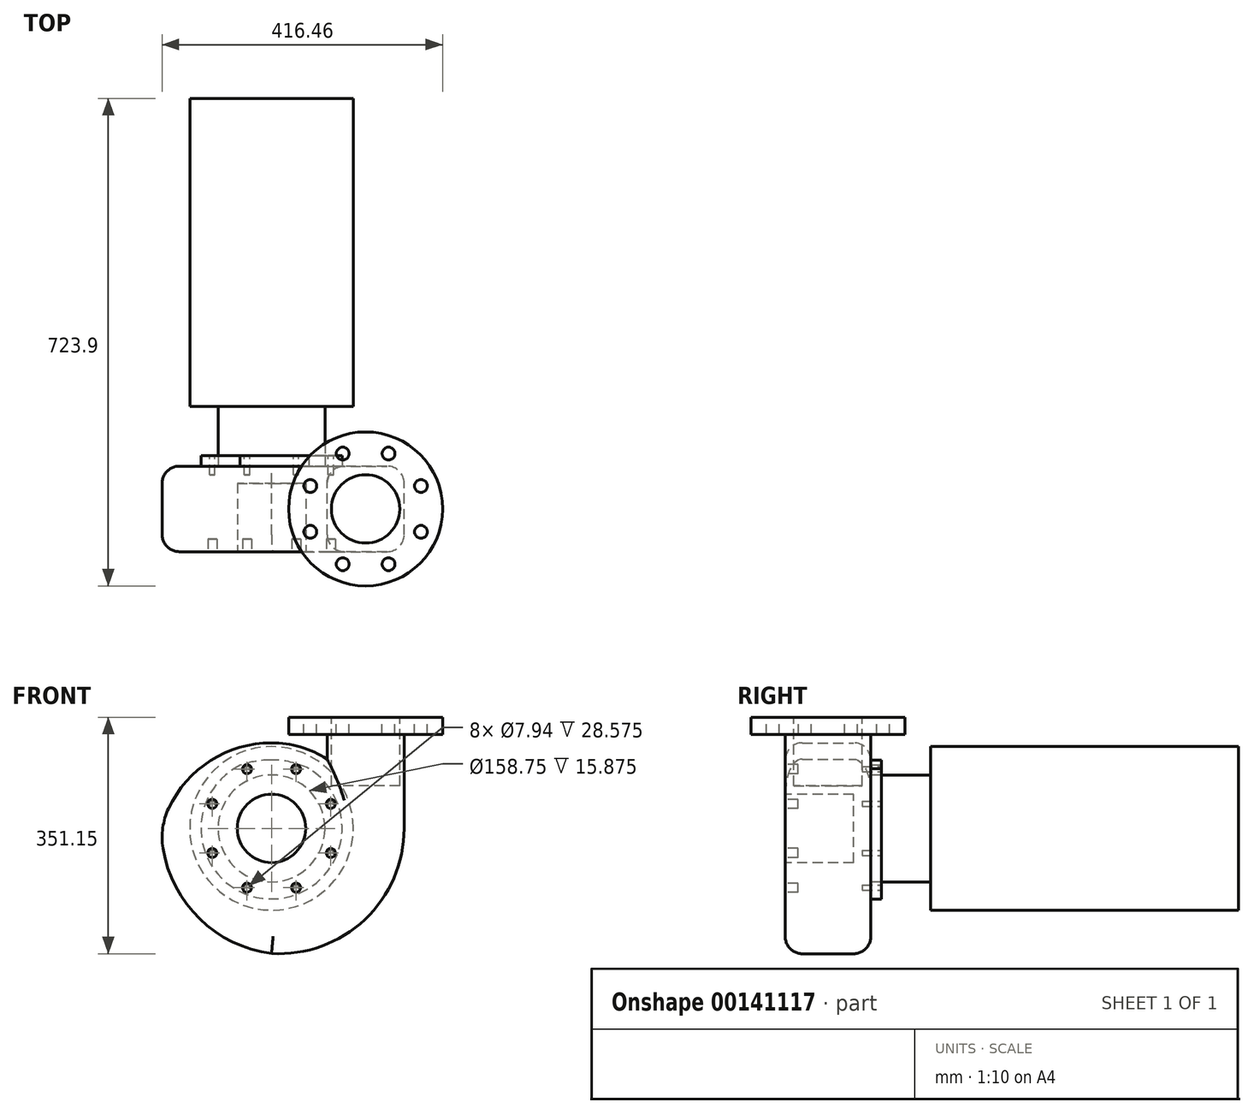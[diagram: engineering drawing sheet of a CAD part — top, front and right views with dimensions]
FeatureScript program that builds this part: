
annotation { "Feature Type Name" : "Feature", "Feature Type Description" : "" }
export const myFeature = defineFeature(function(context is Context, id is Id, definition is map)
    precondition{}
    {
        {
            var Q0;
            Q0=qCreatedBy(makeId("Front.planeOp"),FACE);
            var sketch = newSketch(context, id + "F0", { "sketchPlane" : qUnion([Q0])});
            skLineSegment(sketch, "E0", {"start": v(-163.51, 178.71) * mm, "end": v(-163.51, -178.71) * mm, "construction": true});
            skLineSegment(sketch, "E1", {"start": v(-233.34, 165.1) * mm, "end": v(383.82, 165.1) * mm, "construction": true});
            skLineSegment(sketch, "E2", {"start": v(-286.5, 127) * mm, "end": v(515.42, 127) * mm, "construction": true});
            skLineSegment(sketch, "E3", {"start": v(-378.23, 0) * mm, "end": v(533.77, 0) * mm, "construction": true});
            skLineSegment(sketch, "E4", {"start": v(0, 278.26) * mm, "end": v(0, -265.97) * mm, "construction": true});
            skLineSegment(sketch, "E5", {"start": v(-384.35, -185.74) * mm, "end": v(475.24, -185.74) * mm, "construction": true});
            skLineSegment(sketch, "E6", {"start": v(196.85, 265.15) * mm, "end": v(196.85, -251.12) * mm, "construction": true});
            skPoint(sketch, "E7", {"position": v(0, 0) * mm});
            skArc(sketch, "E8", {"start": v(-163.51, 0) * mm, "mid": v(-116.81, -123.73) * mm, "end": v(0, -185.74) * mm});
            skArc(sketch, "E9", {"start": v(0, -185.74) * mm, "mid": v(138.48, -135.32) * mm, "end": v(196.85, 0) * mm});
            skLineSegment(sketch, "E10", {"start": v(139.7, 277.34) * mm, "end": v(139.7, -312.69) * mm, "construction": true});
            skLineSegment(sketch, "E11", {"start": v(82.55, 361.3) * mm, "end": v(82.55, -345.34) * mm, "construction": true});
            skArc(sketch, "E12", {"start": v(0, 127) * mm, "mid": v(-103.52, 91.52) * mm, "end": v(-163.51, 0) * mm});
            skArc(sketch, "E13", {"start": v(139.7, 36.24) * mm, "mid": v(83.3, 102.32) * mm, "end": v(0, 127) * mm});
            skLineSegment(sketch, "E14", {"start": v(-450.42, 139.7) * mm, "end": v(521.7, 139.7) * mm, "construction": true});
            skLineSegment(sketch, "E15", {"start": v(196.85, 0) * mm, "end": v(196.85, 127) * mm});
            skLineSegment(sketch, "E16", {"start": v(196.85, 127) * mm, "end": v(82.55, 127) * mm});
            skLineSegment(sketch, "E17", {"start": v(82.55, 127) * mm, "end": v(82.55, 102.8) * mm});
            skSolve(sketch);
        }
        {
            var Q0;
            Q0=makeQuery(id+"F0.imprint","IMPRINT",FACE,{"disambiguationData":[TD([[makeQuery(id+"F0.imprint","IMPRINT",EDGE,{"derivedFrom":sQuery(id+"F0.wireOp",EDGE,"E8")}),1.0]])]});
            extrude(context, id + "F1", {"entities" : qUnion([Q0]), "endBound" : BoundingType.SYMMETRIC, "depth" : 127 * mm});
        }
        {
            var Q0;
            Q0=qCreatedBy(makeId("Top.planeOp"),FACE);
            cPlane(context, id + "F2", {"entities" : qUnion([Q0]), "cplaneType" : CPlaneType.OFFSET, "offset" : 165.1 * mm, "width" : 152.4 * mm, "height" : 152.4 * mm});
        }
        {
            var Q0;
            Q0=qCreatedBy(id+"F2.planeOp",FACE);
            var sketch = newSketch(context, id + "F3", { "sketchPlane" : qUnion([Q0])});
            skLineSegment(sketch, "E18", {"start": v(-127.9, 0) * mm, "end": v(189.1, 0) * mm, "construction": true});
            skCircle(sketch, "E19", {"center": v(139.7, 0) * mm, "radius": 50.77 * mm});
            skCircle(sketch, "E20", {"center": v(139.7, 0) * mm, "radius": 114.3 * mm});
            skCircle(sketch, "E21", {"center": v(139.7, 0) * mm, "radius": 88.9 * mm, "construction": true});
            skCircle(sketch, "E22", {"center": v(105.68, 82.13) * mm, "radius": 9.53 * mm});
            skCircle(sketch, "E23.1.0", {"center": v(57.57, 34.02) * mm, "radius": 9.53 * mm});
            skCircle(sketch, "E23.2.0", {"center": v(57.57, -34.02) * mm, "radius": 9.53 * mm});
            skCircle(sketch, "E23.3.0", {"center": v(105.68, -82.13) * mm, "radius": 9.53 * mm});
            skCircle(sketch, "E23.4.0", {"center": v(173.72, -82.13) * mm, "radius": 9.53 * mm});
            skCircle(sketch, "E23.5.0", {"center": v(221.83, -34.02) * mm, "radius": 9.53 * mm});
            skCircle(sketch, "E23.6.0", {"center": v(221.83, 34.02) * mm, "radius": 9.53 * mm});
            skCircle(sketch, "E23.7.0", {"center": v(173.72, 82.13) * mm, "radius": 9.53 * mm});
            skLineSegment(sketch, "E24", {"start": v(105.68, 82.13) * mm, "end": v(173.72, 82.13) * mm, "construction": true});
            skSolve(sketch);
        }
        {
            var Q0;
            Q0=makeQuery(id+"F1.opExtrude","CAP_EDGE",EDGE,{"disambiguationData":[OSD([sQuery(id+"F0.wireOp",EDGE,"E13")])],"isStart":true});
            var Q1;
            Q1=makeQuery(id+"F1.opExtrude","CAP_EDGE",EDGE,{"disambiguationData":[OSD([sQuery(id+"F0.wireOp",EDGE,"E9")])],"isStart":true});
            var Q2;
            Q2=makeQuery(id+"F1.opExtrude","CAP_EDGE",EDGE,{"disambiguationData":[OSD([sQuery(id+"F0.wireOp",EDGE,"E15")])],"isStart":false});
            var Q3;
            Q3=makeQuery(id+"F1.opExtrude","CAP_EDGE",EDGE,{"disambiguationData":[OSD([sQuery(id+"F0.wireOp",EDGE,"E12")])],"isStart":false});
            var Q4;
            Q4=makeQuery(id+"F1.opExtrude","CAP_EDGE",EDGE,{"disambiguationData":[OSD([sQuery(id+"F0.wireOp",EDGE,"E17")])],"isStart":false});
            var Q5;
            Q5=makeQuery(id+"F1.opExtrude","CAP_EDGE",EDGE,{"disambiguationData":[OSD([sQuery(id+"F0.wireOp",EDGE,"E17")])],"isStart":true});
            fillet(context, id + "F4", {"entities" : qUnion([Q0, Q1, Q2, Q3, Q4, Q5]), "radius" : 25.4 * mm, "tangentPropagation" : true, "allowEdgeOverflow" : false});
        }
        {
            var Q0;
            Q0=makeQuery(id+"F3.imprint","IMPRINT",FACE,{"disambiguationData":[TD([[makeQuery(id+"F3.imprint","IMPRINT",EDGE,{"derivedFrom":sQuery(id+"F3.wireOp",EDGE,"E19")}),-1.0]])]});
            extrude(context, id + "F5", {"entities" : qUnion([Q0]), "oppositeDirection" : true, "depth" : 25.4 * mm});
        }
        {
            var Q0;
            Q0=makeQuery(id+"F3.imprint","IMPRINT",FACE,{"disambiguationData":[TD([[makeQuery(id+"F3.imprint","IMPRINT",EDGE,{"derivedFrom":sQuery(id+"F3.wireOp",EDGE,"E19")}),1.0]])]});
            extrude(context, id + "F6", {"entities" : qUnion([Q0]), "operationType" : NewBodyOperationType.REMOVE, "oppositeDirection" : true, "depth" : 101.6 * mm});
        }
        {
            var Q0;
            Q0=makeQuery(id+"F1.opExtrude","SWEPT_FACE",FACE,{"disambiguationData":[OSD([sQuery(id+"F0.wireOp",EDGE,"E16")])]});
            var Q1;
            Q1=makeQuery(id+"F5.opExtrude","SWEPT_BODY",BODY,{"disambiguationData":[OSD([sQuery(id+"F3.wireOp",EDGE,"E19"),sQuery(id+"F3.wireOp",EDGE,"E20")])]});
            extrude(context, id + "F7", {"entities" : qUnion([Q0]), "operationType" : NewBodyOperationType.ADD, "endBound" : BoundingType.UP_TO_BODY, "endBoundEntityBody" : qUnion([Q1]), "depth" : 25.4 * mm});
        }
        {
            var Q0;
            Q0=makeQuery(id+"F1.opExtrude","SWEPT_EDGE",EDGE,{"disambiguationData":[OSD([sQuery(id+"F0.wireOp",EDGE,"E8"),sQuery(id+"F0.wireOp",EDGE,"E12")])]});
            fillet(context, id + "F8", {"entities" : qUnion([Q0]), "radius" : 101.6 * mm, "tangentPropagation" : true, "allowEdgeOverflow" : false});
        }
        {
            var Q0;
            {var subQ0=sQuery(id+"F0.wireOp",EDGE,"E16");Q0=makeQuery(id+"F7.boolean.opBoolean","MERGE",FACE,{"derivedFrom":[makeQuery(id+"F1.opExtrude","CAP_FACE",FACE,{"disambiguationData":[OSD([sQuery(id+"F0.wireOp",EDGE,"E8"),sQuery(id+"F0.wireOp",EDGE,"E9"),sQuery(id+"F0.wireOp",EDGE,"E12"),sQuery(id+"F0.wireOp",EDGE,"E13"),sQuery(id+"F0.wireOp",EDGE,"E15"),subQ0,sQuery(id+"F0.wireOp",EDGE,"E17")])],"isStart":false}),makeQuery(id+"F7.opExtrude","SWEPT_FACE",FACE,{"disambiguationData":[OSD([subQ0]),TDD([makeQuery(id+"F1.opExtrude","CAP_EDGE",EDGE,{"disambiguationData":[OSD([subQ0])],"isStart":false})])]})]});}
            var sketch = newSketch(context, id + "F9", { "sketchPlane" : qUnion([Q0])});
            skCircle(sketch, "E25", {"center": v(0, 0) * mm, "radius": 50.77 * mm});
            skCircle(sketch, "E26", {"center": v(0, 0) * mm, "radius": 95.25 * mm, "construction": true});
            skCircle(sketch, "E27", {"center": v(-36.45, 88) * mm, "radius": 6.75 * mm});
            skCircle(sketch, "E28.1.0", {"center": v(-88, 36.45) * mm, "radius": 6.75 * mm});
            skCircle(sketch, "E28.2.0", {"center": v(-88, -36.45) * mm, "radius": 6.75 * mm});
            skCircle(sketch, "E28.3.0", {"center": v(-36.45, -88) * mm, "radius": 6.75 * mm});
            skCircle(sketch, "E28.4.0", {"center": v(36.45, -88) * mm, "radius": 6.75 * mm});
            skCircle(sketch, "E28.5.0", {"center": v(88, -36.45) * mm, "radius": 6.75 * mm});
            skCircle(sketch, "E28.6.0", {"center": v(88, 36.45) * mm, "radius": 6.75 * mm});
            skCircle(sketch, "E28.7.0", {"center": v(36.45, 88) * mm, "radius": 6.75 * mm});
            skLineSegment(sketch, "E29", {"start": v(-36.45, 88) * mm, "end": v(36.45, 88) * mm, "construction": true});
            skSolve(sketch);
        }
        {
            var Q0;
            Q0=makeQuery(id+"F9.imprint","IMPRINT",FACE,{"disambiguationData":[TD([[makeQuery(id+"F9.imprint","IMPRINT",EDGE,{"derivedFrom":sQuery(id+"F9.wireOp",EDGE,"E27")}),1.0]])]});
            var Q1;
            Q1=makeQuery(id+"F9.imprint","IMPRINT",FACE,{"disambiguationData":[TD([[makeQuery(id+"F9.imprint","IMPRINT",EDGE,{"derivedFrom":sQuery(id+"F9.wireOp",EDGE,"E28.7.0")}),1.0]])]});
            var Q2;
            Q2=makeQuery(id+"F9.imprint","IMPRINT",FACE,{"disambiguationData":[TD([[makeQuery(id+"F9.imprint","IMPRINT",EDGE,{"derivedFrom":sQuery(id+"F9.wireOp",EDGE,"E28.6.0")}),1.0]])]});
            var Q3;
            Q3=makeQuery(id+"F9.imprint","IMPRINT",FACE,{"disambiguationData":[TD([[makeQuery(id+"F9.imprint","IMPRINT",EDGE,{"derivedFrom":sQuery(id+"F9.wireOp",EDGE,"E28.5.0")}),1.0]])]});
            var Q4;
            Q4=makeQuery(id+"F9.imprint","IMPRINT",FACE,{"disambiguationData":[TD([[makeQuery(id+"F9.imprint","IMPRINT",EDGE,{"derivedFrom":sQuery(id+"F9.wireOp",EDGE,"E28.4.0")}),1.0]])]});
            var Q5;
            Q5=makeQuery(id+"F9.imprint","IMPRINT",FACE,{"disambiguationData":[TD([[makeQuery(id+"F9.imprint","IMPRINT",EDGE,{"derivedFrom":sQuery(id+"F9.wireOp",EDGE,"E28.3.0")}),1.0]])]});
            var Q6;
            Q6=makeQuery(id+"F9.imprint","IMPRINT",FACE,{"disambiguationData":[TD([[makeQuery(id+"F9.imprint","IMPRINT",EDGE,{"derivedFrom":sQuery(id+"F9.wireOp",EDGE,"E28.2.0")}),1.0]])]});
            var Q7;
            Q7=makeQuery(id+"F9.imprint","IMPRINT",FACE,{"disambiguationData":[TD([[makeQuery(id+"F9.imprint","IMPRINT",EDGE,{"derivedFrom":sQuery(id+"F9.wireOp",EDGE,"E28.1.0")}),1.0]])]});
            extrude(context, id + "F10", {"entities" : qUnion([Q0, Q1, Q2, Q3, Q4, Q5, Q6, Q7]), "operationType" : NewBodyOperationType.REMOVE, "oppositeDirection" : true, "depth" : 19.05 * mm});
        }
        {
            var Q0;
            Q0=makeQuery(id+"F9.imprint","IMPRINT",FACE,{"disambiguationData":[TD([[makeQuery(id+"F9.imprint","IMPRINT",EDGE,{"derivedFrom":sQuery(id+"F9.wireOp",EDGE,"E25")}),1.0]])]});
            extrude(context, id + "F11", {"entities" : qUnion([Q0]), "operationType" : NewBodyOperationType.REMOVE, "oppositeDirection" : true, "depth" : 101.6 * mm});
        }
        {
            var Q0;
            {var subQ0=sQuery(id+"F0.wireOp",EDGE,"E16");Q0=makeQuery(id+"F7.boolean.opBoolean","MERGE",FACE,{"derivedFrom":[makeQuery(id+"F1.opExtrude","CAP_FACE",FACE,{"disambiguationData":[OSD([sQuery(id+"F0.wireOp",EDGE,"E8"),sQuery(id+"F0.wireOp",EDGE,"E9"),sQuery(id+"F0.wireOp",EDGE,"E12"),sQuery(id+"F0.wireOp",EDGE,"E13"),sQuery(id+"F0.wireOp",EDGE,"E15"),subQ0,sQuery(id+"F0.wireOp",EDGE,"E17")])],"isStart":true}),makeQuery(id+"F7.opExtrude","SWEPT_FACE",FACE,{"disambiguationData":[OSD([subQ0]),TDD([makeQuery(id+"F1.opExtrude","CAP_EDGE",EDGE,{"disambiguationData":[OSD([subQ0])],"isStart":true})])]})]});}
            var sketch = newSketch(context, id + "F12", { "sketchPlane" : qUnion([Q0])});
            skCircle(sketch, "E30", {"center": v(0, 0) * mm, "radius": 95.25 * mm, "construction": true});
            skCircle(sketch, "E31", {"center": v(-36.45, 88) * mm, "radius": 3.97 * mm});
            skCircle(sketch, "E32.1.0", {"center": v(-88, 36.45) * mm, "radius": 3.97 * mm});
            skCircle(sketch, "E32.2.0", {"center": v(-88, -36.45) * mm, "radius": 3.97 * mm});
            skCircle(sketch, "E32.3.0", {"center": v(-36.45, -88) * mm, "radius": 3.97 * mm});
            skCircle(sketch, "E32.4.0", {"center": v(36.45, -88) * mm, "radius": 3.97 * mm});
            skCircle(sketch, "E32.5.0", {"center": v(88, -36.45) * mm, "radius": 3.97 * mm});
            skCircle(sketch, "E32.6.0", {"center": v(88, 36.45) * mm, "radius": 3.97 * mm});
            skCircle(sketch, "E32.7.0", {"center": v(36.45, 88) * mm, "radius": 3.97 * mm});
            skLineSegment(sketch, "E33", {"start": v(-36.45, 88) * mm, "end": v(36.45, 88) * mm, "construction": true});
            skCircle(sketch, "E34", {"center": v(0, 0) * mm, "radius": 104.78 * mm});
            skCircle(sketch, "E35", {"center": v(0, 0) * mm, "radius": 79.38 * mm});
            skSolve(sketch);
        }
        {
            var Q0;
            Q0=makeQuery(id+"F12.imprint","IMPRINT",FACE,{"disambiguationData":[TD([[makeQuery(id+"F12.imprint","IMPRINT",EDGE,{"derivedFrom":sQuery(id+"F12.wireOp",EDGE,"E32.1.0")}),1.0]])]});
            var Q1;
            Q1=makeQuery(id+"F12.imprint","IMPRINT",FACE,{"disambiguationData":[TD([[makeQuery(id+"F12.imprint","IMPRINT",EDGE,{"derivedFrom":sQuery(id+"F12.wireOp",EDGE,"E31")}),1.0]])]});
            var Q2;
            Q2=makeQuery(id+"F12.imprint","IMPRINT",FACE,{"disambiguationData":[TD([[makeQuery(id+"F12.imprint","IMPRINT",EDGE,{"derivedFrom":sQuery(id+"F12.wireOp",EDGE,"E32.7.0")}),1.0]])]});
            var Q3;
            Q3=makeQuery(id+"F12.imprint","IMPRINT",FACE,{"disambiguationData":[TD([[makeQuery(id+"F12.imprint","IMPRINT",EDGE,{"derivedFrom":sQuery(id+"F12.wireOp",EDGE,"E32.6.0")}),1.0]])]});
            var Q4;
            Q4=makeQuery(id+"F12.imprint","IMPRINT",FACE,{"disambiguationData":[TD([[makeQuery(id+"F12.imprint","IMPRINT",EDGE,{"derivedFrom":sQuery(id+"F12.wireOp",EDGE,"E32.5.0")}),1.0]])]});
            var Q5;
            Q5=makeQuery(id+"F12.imprint","IMPRINT",FACE,{"disambiguationData":[TD([[makeQuery(id+"F12.imprint","IMPRINT",EDGE,{"derivedFrom":sQuery(id+"F12.wireOp",EDGE,"E32.4.0")}),1.0]])]});
            var Q6;
            Q6=makeQuery(id+"F12.imprint","IMPRINT",FACE,{"disambiguationData":[TD([[makeQuery(id+"F12.imprint","IMPRINT",EDGE,{"derivedFrom":sQuery(id+"F12.wireOp",EDGE,"E32.3.0")}),1.0]])]});
            var Q7;
            Q7=makeQuery(id+"F12.imprint","IMPRINT",FACE,{"disambiguationData":[TD([[makeQuery(id+"F12.imprint","IMPRINT",EDGE,{"derivedFrom":sQuery(id+"F12.wireOp",EDGE,"E32.2.0")}),1.0]])]});
            extrude(context, id + "F13", {"entities" : qUnion([Q0, Q1, Q2, Q3, Q4, Q5, Q6, Q7]), "operationType" : NewBodyOperationType.REMOVE, "oppositeDirection" : true, "depth" : 12.7 * mm});
        }
        {
            var Q0;
            Q0=makeQuery(id+"F12.imprint","IMPRINT",FACE,{"disambiguationData":[TD([[makeQuery(id+"F12.imprint","IMPRINT",EDGE,{"derivedFrom":sQuery(id+"F12.wireOp",EDGE,"E31")}),-1.0]])]});
            extrude(context, id + "F14", {"entities" : qUnion([Q0]), "operationType" : NewBodyOperationType.ADD, "depth" : 15.88 * mm});
        }
        {
            var Q0;
            Q0=makeQuery(id+"F12.imprint","IMPRINT",FACE,{"disambiguationData":[TD([[makeQuery(id+"F12.imprint","IMPRINT",EDGE,{"derivedFrom":sQuery(id+"F12.wireOp",EDGE,"E35")}),1.0]])]});
            cPlane(context, id + "F15", {"entities" : qUnion([Q0]), "cplaneType" : CPlaneType.OFFSET, "offset" : 88.9 * mm, "width" : 152.4 * mm, "height" : 152.4 * mm});
        }
        {
            var Q0;
            Q0=makeQuery(id+"F14.opExtrude","CAP_FACE",FACE,{"disambiguationData":[OSD([sQuery(id+"F0.wireOp",EDGE,"E8"),sQuery(id+"F0.wireOp",EDGE,"E9"),sQuery(id+"F0.wireOp",EDGE,"E12"),sQuery(id+"F0.wireOp",EDGE,"E13"),sQuery(id+"F0.wireOp",EDGE,"E15"),sQuery(id+"F0.wireOp",EDGE,"E16"),sQuery(id+"F0.wireOp",EDGE,"E17"),sQuery(id+"F12.wireOp",EDGE,"E31"),sQuery(id+"F12.wireOp",EDGE,"E32.1.0"),sQuery(id+"F12.wireOp",EDGE,"E32.2.0"),sQuery(id+"F12.wireOp",EDGE,"E32.3.0"),sQuery(id+"F12.wireOp",EDGE,"E32.4.0"),sQuery(id+"F12.wireOp",EDGE,"E32.5.0"),sQuery(id+"F12.wireOp",EDGE,"E32.6.0"),sQuery(id+"F12.wireOp",EDGE,"E32.7.0"),sQuery(id+"F12.wireOp",EDGE,"E34"),sQuery(id+"F12.wireOp",EDGE,"E35")])],"isStart":false});
            var sketch = newSketch(context, id + "F16", { "sketchPlane" : qUnion([Q0])});
            skLineSegment(sketch, "E36", {"start": v(0, 118.05) * mm, "end": v(0, -125.44) * mm, "construction": true});
            skLineSegment(sketch, "E37.bottom", {"start": v(-9.53, 101.6) * mm, "end": v(9.53, 101.6) * mm});
            skLineSegment(sketch, "E37.top", {"start": v(-9.52, 79.38) * mm, "end": v(9.52, 79.38) * mm});
            skLineSegment(sketch, "E37.left", {"start": v(-9.53, 101.6) * mm, "end": v(-9.52, 79.38) * mm});
            skLineSegment(sketch, "E37.right", {"start": v(9.53, 101.6) * mm, "end": v(9.53, 79.38) * mm});
            skCircle(sketch, "E38.0", {"center": v(0, 0) * mm, "radius": 79.38 * mm});
            skCircle(sketch, "E39.0", {"center": v(0, 0) * mm, "radius": 104.78 * mm});
            skLineSegment(sketch, "E40.1.0", {"start": v(-101.6, 9.53) * mm, "end": v(-79.38, 9.53) * mm});
            skLineSegment(sketch, "E40.1.1", {"start": v(-101.6, -9.52) * mm, "end": v(-79.38, -9.52) * mm});
            skLineSegment(sketch, "E40.1.2", {"start": v(-101.6, -9.52) * mm, "end": v(-101.6, 9.53) * mm});
            skLineSegment(sketch, "E40.1.3", {"start": v(-79.38, -9.52) * mm, "end": v(-79.38, 9.53) * mm});
            skLineSegment(sketch, "E40.2.0", {"start": v(-9.53, -101.6) * mm, "end": v(-9.53, -79.38) * mm});
            skLineSegment(sketch, "E40.2.1", {"start": v(9.52, -101.6) * mm, "end": v(9.52, -79.38) * mm});
            skLineSegment(sketch, "E40.2.2", {"start": v(9.52, -101.6) * mm, "end": v(-9.53, -101.6) * mm});
            skLineSegment(sketch, "E40.2.3", {"start": v(9.52, -79.38) * mm, "end": v(-9.53, -79.38) * mm});
            skLineSegment(sketch, "E40.3.0", {"start": v(101.6, -9.53) * mm, "end": v(79.38, -9.53) * mm});
            skLineSegment(sketch, "E40.3.1", {"start": v(101.6, 9.52) * mm, "end": v(79.38, 9.52) * mm});
            skLineSegment(sketch, "E40.3.2", {"start": v(101.6, 9.52) * mm, "end": v(101.6, -9.53) * mm});
            skLineSegment(sketch, "E40.3.3", {"start": v(79.38, 9.52) * mm, "end": v(79.38, -9.53) * mm});
            skSolve(sketch);
        }
        {
            var Q0;
            Q0=qCreatedBy(id+"F15.planeOp",FACE);
            var sketch = newSketch(context, id + "F17", { "sketchPlane" : qUnion([Q0])});
            skCircle(sketch, "E41", {"center": v(0, 0) * mm, "radius": 121.44 * mm});
            skSolve(sketch);
        }
        {
            var Q0;
            Q0=makeQuery(id+"F17.imprint","IMPRINT",FACE,{"disambiguationData":[TD([[makeQuery(id+"F17.imprint","IMPRINT",EDGE,{"derivedFrom":sQuery(id+"F17.wireOp",EDGE,"E41")}),1.0]])]});
            extrude(context, id + "F18", {"entities" : qUnion([Q0]), "depth" : 457.2 * mm});
        }
        {
            var Q0;
            {var subQ0=sQuery(id+"F16.wireOp",EDGE,"E38.0");var subQ1=makeQuery(id+"F16.imprint","INTERSECT",VERTEX,{"derivedFrom":[sQuery(id+"F16.wireOp",EDGE,"E37.top"),subQ0]});Q0=makeQuery(id+"F16.imprint","IMPRINT",FACE,{"disambiguationData":[TD([[makeQuery(id+"F16.imprint","IMPRINT",EDGE,{"disambiguationData":[TD([[subQ1,1.0]])],"derivedFrom":subQ0}),1.0]])]});}
            var Q1;
            Q1=sQuery(id+"F16.wireOp",EDGE,"E38.0");
            var Q2;
            Q2=makeQuery(id+"F18.opExtrude","SWEPT_BODY",BODY,{"disambiguationData":[OSD([sQuery(id+"F17.wireOp",EDGE,"E41")])]});
            extrude(context, id + "F19", {"entities" : qUnion([Q0]), "operationType" : NewBodyOperationType.ADD, "surfaceEntities" : qUnion([Q1]), "endBound" : BoundingType.UP_TO_BODY, "endBoundEntityBody" : qUnion([Q2]), "depth" : 25.4 * mm});
        }
    });
